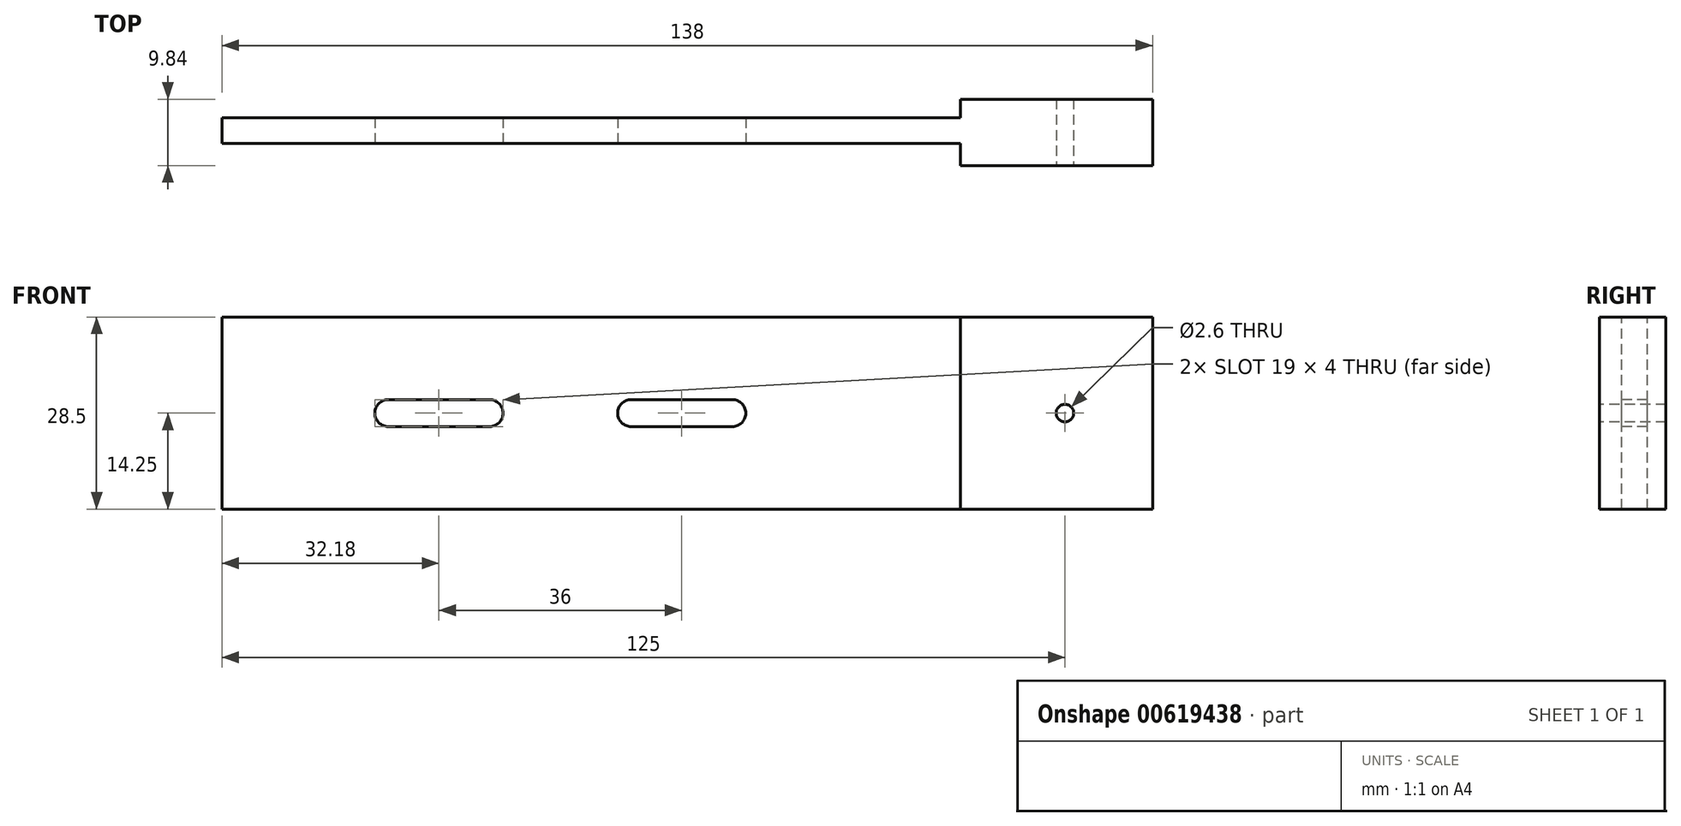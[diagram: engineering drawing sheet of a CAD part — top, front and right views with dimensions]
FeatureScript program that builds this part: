
annotation { "Feature Type Name" : "Feature", "Feature Type Description" : "" }
export const myFeature = defineFeature(function(context is Context, id is Id, definition is map)
    precondition{}
    {
        {
            var Q0;
            Q0=qCreatedBy(makeId("Front.planeOp"),FACE);
            var sketch = newSketch(context, id + "F0", { "sketchPlane" : qUnion([Q0])});
            skLineSegment(sketch, "E0.bottom", {"start": v(0, 0) * mm, "end": v(138, 0) * mm});
            skLineSegment(sketch, "E0.top", {"start": v(0, 28.5) * mm, "end": v(138, 28.5) * mm});
            skLineSegment(sketch, "E0.left", {"start": v(0, 0) * mm, "end": v(0, 28.5) * mm});
            skLineSegment(sketch, "E0.right", {"start": v(138, 0) * mm, "end": v(138, 28.5) * mm});
            skSolve(sketch);
        }
        {
            var Q0;
            Q0 = qSketchRegion(id + "F0", true);
            extrude(context, id + "F1", {"entities" : qUnion([Q0]), "depth" : 3.8 * mm, "offsetDistance" : 25 * mm});
        }
        {
            var Q0;
            Q0=makeQuery(id+"F1.opExtrude","CAP_FACE",FACE,{"disambiguationData":[OSD([sQuery(id+"F0.wireOp",EDGE,"E0.bottom"),sQuery(id+"F0.wireOp",EDGE,"E0.top"),sQuery(id+"F0.wireOp",EDGE,"E0.left"),sQuery(id+"F0.wireOp",EDGE,"E0.right")])],"isStart":false});
            var sketch = newSketch(context, id + "F2", { "sketchPlane" : qUnion([Q0])});
            skLineSegment(sketch, "E1.bottom", {"start": v(138, 28.5) * mm, "end": v(109.5, 28.5) * mm});
            skLineSegment(sketch, "E1.top", {"start": v(138, 0) * mm, "end": v(109.5, 0) * mm});
            skLineSegment(sketch, "E1.left", {"start": v(138, 28.5) * mm, "end": v(138, 0) * mm});
            skLineSegment(sketch, "E1.right", {"start": v(109.5, 28.5) * mm, "end": v(109.5, 0) * mm});
            skSolve(sketch);
        }
        {
            var Q0;
            Q0 = qSketchRegion(id + "F2", true);
            extrude(context, id + "F3", {"entities" : qUnion([Q0]), "operationType" : NewBodyOperationType.ADD, "depth" : 3.28 * mm, "offsetDistance" : 25 * mm, "hasSecondDirection" : true, "secondDirectionOppositeDirection" : true, "secondDirectionDepth" : 6.56 * mm});
        }
        {
            var Q0;
            Q0=makeQuery(id+"F1.opExtrude","CAP_FACE",FACE,{"disambiguationData":[OSD([sQuery(id+"F0.wireOp",EDGE,"E0.bottom"),sQuery(id+"F0.wireOp",EDGE,"E0.top"),sQuery(id+"F0.wireOp",EDGE,"E0.left"),sQuery(id+"F0.wireOp",EDGE,"E0.right")])],"isStart":false});
            var sketch = newSketch(context, id + "F4", { "sketchPlane" : qUnion([Q0])});
            skLineSegment(sketch, "E2", {"start": v(0, 14.25) * mm, "end": v(125, 14.25) * mm});
            skLineSegment(sketch, "E3.bottom", {"start": v(75.68, 16.25) * mm, "end": v(60.68, 16.25) * mm});
            skLineSegment(sketch, "E3.top", {"start": v(75.68, 12.25) * mm, "end": v(60.68, 12.25) * mm});
            skLineSegment(sketch, "E3.left", {"start": v(77.68, 14.25) * mm, "end": v(77.68, 14.25) * mm});
            skLineSegment(sketch, "E3.right", {"start": v(58.68, 14.25) * mm, "end": v(58.68, 14.25) * mm});
            skLineSegment(sketch, "E4.bottom", {"start": v(24.68, 16.25) * mm, "end": v(39.68, 16.25) * mm});
            skLineSegment(sketch, "E4.top", {"start": v(24.68, 12.25) * mm, "end": v(39.68, 12.25) * mm});
            skLineSegment(sketch, "E4.left", {"start": v(22.68, 14.25) * mm, "end": v(22.68, 14.25) * mm});
            skLineSegment(sketch, "E4.right", {"start": v(41.68, 14.25) * mm, "end": v(41.68, 14.25) * mm});
            skPoint(sketch, "E5.visualSharp", {"position": v(58.68, 16.25) * mm});
            skArc(sketch, "E5.filletArc", {"start": v(60.68, 16.25) * mm, "mid": v(59.27, 15.66) * mm, "end": v(58.68, 14.25) * mm});
            skPoint(sketch, "E6.visualSharp", {"position": v(58.68, 12.25) * mm});
            skArc(sketch, "E6.filletArc", {"start": v(58.68, 14.25) * mm, "mid": v(59.27, 12.84) * mm, "end": v(60.68, 12.25) * mm});
            skPoint(sketch, "E7.visualSharp", {"position": v(77.68, 16.25) * mm});
            skArc(sketch, "E7.filletArc", {"start": v(77.68, 14.25) * mm, "mid": v(77.1, 15.66) * mm, "end": v(75.68, 16.25) * mm});
            skPoint(sketch, "E8.visualSharp", {"position": v(77.68, 12.25) * mm});
            skArc(sketch, "E8.filletArc", {"start": v(75.68, 12.25) * mm, "mid": v(77.1, 12.84) * mm, "end": v(77.68, 14.25) * mm});
            skPoint(sketch, "E9.visualSharp", {"position": v(41.68, 16.25) * mm});
            skArc(sketch, "E9.filletArc", {"start": v(41.68, 14.25) * mm, "mid": v(41.1, 15.66) * mm, "end": v(39.68, 16.25) * mm});
            skPoint(sketch, "E10.visualSharp", {"position": v(41.68, 12.25) * mm});
            skArc(sketch, "E10.filletArc", {"start": v(39.68, 12.25) * mm, "mid": v(41.1, 12.84) * mm, "end": v(41.68, 14.25) * mm});
            skPoint(sketch, "E11.visualSharp", {"position": v(22.68, 16.25) * mm});
            skArc(sketch, "E11.filletArc", {"start": v(24.68, 16.25) * mm, "mid": v(23.27, 15.66) * mm, "end": v(22.68, 14.25) * mm});
            skPoint(sketch, "E12.visualSharp", {"position": v(22.68, 12.25) * mm});
            skArc(sketch, "E12.filletArc", {"start": v(22.68, 14.25) * mm, "mid": v(23.27, 12.84) * mm, "end": v(24.68, 12.25) * mm});
            skLineSegment(sketch, "E13", {"start": v(125, 39.5) * mm, "end": v(125, -8.7) * mm});
            skPoint(sketch, "E14.orphan", {"position": v(109.5, 14.25) * mm});
            skSolve(sketch);
        }
        {
            var Q0;
            Q0=makeQuery(id+"F3.opExtrude","CAP_FACE",FACE,{"disambiguationData":[OSD([sQuery(id+"F2.wireOp",EDGE,"E1.bottom"),sQuery(id+"F2.wireOp",EDGE,"E1.top"),sQuery(id+"F2.wireOp",EDGE,"E1.left"),sQuery(id+"F2.wireOp",EDGE,"E1.right")])],"isStart":false});
            var sketch = newSketch(context, id + "F5", { "sketchPlane" : qUnion([Q0])});
            skCircle(sketch, "E15", {"center": v(125, 14.25) * mm, "radius": 1.3 * mm});
            skSolve(sketch);
        }
        {
            var Q0;
            Q0=makeQuery(id+"F5.imprint","IMPRINT",FACE,{"disambiguationData":[TD([[makeQuery(id+"F5.imprint","IMPRINT",EDGE,{"derivedFrom":sQuery(id+"F5.wireOp",EDGE,"E15")}),1.0]])]});
            extrude(context, id + "F6", {"entities" : qUnion([Q0]), "operationType" : NewBodyOperationType.REMOVE, "endBound" : BoundingType.UP_TO_NEXT, "oppositeDirection" : true, "depth" : 25 * mm, "offsetDistance" : 25 * mm});
        }
        {
            var Q0;
            Q0 = qSketchRegion(id + "F4", true);
            extrude(context, id + "F7", {"entities" : qUnion([Q0]), "operationType" : NewBodyOperationType.REMOVE, "endBound" : BoundingType.UP_TO_NEXT, "oppositeDirection" : true, "depth" : 25 * mm, "offsetDistance" : 25 * mm});
        }
    });
